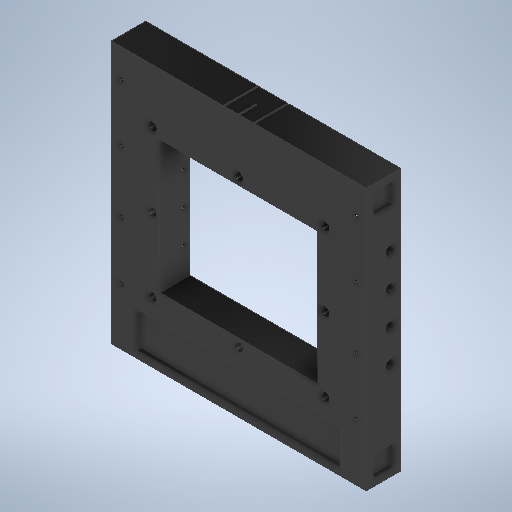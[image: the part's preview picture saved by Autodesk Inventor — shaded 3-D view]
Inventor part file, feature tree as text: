
AUTODESK INVENTOR PART (.ipt)
format: ipt  version: 2025.1 (Build 291241000, 241)  size: 1,624,064 bytes
history: native  units: mm
features: extrude x28, sketch x11, plane x1
ambient origin geometry x8: Origin, YZ Plane, XZ Plane, XY Plane, X Axis, Y Axis, Z Axis, Center Point
bodies: Volumenkörper1 (feature_tree)
feature tree (40):
  extrude  "Extrusion1"  Depth=178.0mm
  extrude  "Extrusion2"  Depth=2.0mm
  extrude  "Extrusion3"  Depth=17.0mm
  extrude  "Extrusion4"  Depth=156.5mm TaperAngle=0.0deg
  extrude  "Extrusion5"  TaperAngle=45.0deg  [1 undecoded]
  extrude  "Extrusion6"  TaperAngle=45.0deg  [1 undecoded]
  extrude  "Extrusion7"  Depth=181.0mm TaperAngle=0.0deg
  extrude  "Extrusion8"  Depth=5.0mm TaperAngle=0.0deg
  plane  "Arbeitsebene1"
  extrude  "Extrusion9"  Depth=5.0mm
  extrude  "Extrusion10"  Depth=150.7mm
  extrude  "Extrusion11"  Depth=3.0mm TaperAngle=0.0deg
  extrude  "Extrusion12"  TaperAngle=0.0deg  [1 undecoded]
  extrude  "Extrusion13"  Depth=5.0mm
  extrude  "Extrusion14"  Depth=5.0mm
  extrude  "Extrusion15"  Depth=5.0mm
  extrude  "Extrusion16"  Depth=5.0mm
  extrude  "Extrusion17"  Depth=3.0mm TaperAngle=0.0deg
  extrude  "Extrusion20"  Depth=5.0mm
  extrude  "Extrusion21"  Depth=5.0mm
  extrude  "Extrusion22"  Depth=5.0mm
  extrude  "Extrusion23"  Depth=5.0mm
  extrude  "Extrusion24"  Depth=3.0mm TaperAngle=0.0deg
  extrude  "Extrusion25"  Depth=3.0mm TaperAngle=0.0deg
  extrude  "Extrusion26"  Depth=5.0mm
  extrude  "Extrusion27"  Depth=5.0mm
  extrude  "Extrusion28"  Depth=3.0mm
  extrude  "Extrusion29"  Depth=3.0mm
  extrude  "Extrusion30"  Depth=5.0mm TaperAngle=0.0deg
  sketch  "Skizze3"  dims[d0=183.0mm d1=178.0mm]
  sketch  "Skizze9"  dims[d2=24.0mm d3=0.0mm d4=2.0mm]
  sketch  "Skizze10"  dims[d5=2.0mm d6=17.0mm]
  sketch  "Skizze11"  dims[d7=24.0mm d8=156.5mm d9=0.0mm]
  sketch  "Skizze12"  dims[d10=5.0mm d11=45.0deg]
  sketch  "Skizze14"  dims[d12=45.0deg d13=45.0deg]
  sketch  "Skizze30"  dims[d14=45.0deg d15=181.0mm d16=0.0mm]
  sketch  "Skizze36"  dims[d17=5.0mm d18=0.0mm d19=2.0mm d20=0.0mm]
  sketch  "Skizze42"  dims[d21=5.0mm d22=24.0mm]
  sketch  "Skizze45"  dims[d23=24.0mm d24=150.7mm]
  sketch  "Skizze47"  dims[d25=133.0mm d26=3.0mm d27=0.0mm d36=0.0mm d37=0.0mm d38=24.0mm d39=24.0mm d40=14.0mm d41=14.0mm d42=3.0mm d43=0.0mm d44=5.0mm d45=24.5mm d46=6.0mm d47=6.0mm d48=3.0mm d49=0.0mm d50=3.0mm d51=0.0mm d52=2.0mm d53=24.5mm d54=3.0mm d55=3.0mm d56=181.0mm d57=0.0mm d58=20.0mm d59=10.0mm d60=10.0mm d61=10.0mm d62=10.0mm d63=10.0mm d64=10.0mm d65=10.0mm d66=10.0mm d67=10.0mm d68=10.0mm d69=10.0mm d70=10.0mm d71=10.0mm d72=8.0mm d73=2.0mm d74=2.0mm d75=8.0mm d76=2.0mm d77=2.0mm d78=114.0mm d79=0.0mm d80=178.0mm d81=14.5mm d82=1.0mm d83=1.0mm d84=154.0mm d85=154.0mm d86=1.0mm d87=0.0mm d88=1.0mm d89=0.0mm d90=130.0mm d91=130.0mm d94=1.0mm d98=3.0mm d99=0.0mm d100=3.0mm d101=0.0mm d102=3.0mm d103=0.0mm d105=92.5mm d106=110.2mm d107=15.0mm d108=15.0mm d109=15.0mm d110=15.0mm d112=3.4mm d113=3.4mm d114=3.4mm d115=3.4mm d116=3.4mm d117=3.4mm d118=3.4mm d119=0.0mm d120=0.0mm d121=0.0mm d122=0.0mm d123=0.0mm d125=0.0mm d126=0.0mm d127=0.0mm d128=0.0mm d129=0.0mm d130=0.0mm d131=3.4mm d132=120.7mm d133=103.0mm d134=2.5mm d140=24.0mm d141=24.0mm d142=24.0mm d143=24.0mm d144=24.0mm d145=24.0mm d146=24.0mm d147=5.0mm d148=0.0mm d161=5.0mm d162=5.0mm d163=5.0mm d164=5.0mm d165=5.0mm d166=5.0mm d167=5.0mm d168=5.0mm d169=14.0mm d170=14.0mm d171=14.0mm d172=14.0mm d173=14.0mm d174=14.0mm d175=14.0mm d176=14.0mm d177=3.0mm d178=0.0mm d179=20.0mm d180=2.0mm d181=2.0mm d182=1.0mm d183=0.0mm d184=20.0mm d185=0.0mm d186=130.0mm d187=14.0mm d188=6.0mm d189=6.0mm d190=6.0mm d191=6.0mm d192=6.0mm d193=6.0mm d194=6.0mm d195=6.0mm d196=20.0mm d197=0.0mm d198=168.5mm d199=0.0mm d200=5.0mm d201=0.0mm d202=5.7mm d203=12.0mm d204=12.0mm d205=20.0mm d206=40.0mm d207=40.0mm d208=40.0mm d209=5.7mm d210=5.7mm d211=5.7mm d212=3.4mm d213=3.4mm d214=3.4mm d215=3.4mm d216=3.4mm d217=3.4mm d218=3.4mm d219=3.4mm d220=0.0mm d221=0.0mm d222=0.0mm d223=0.0mm d224=6.0mm d225=6.0mm d226=6.0mm d227=6.0mm d228=6.0mm d229=6.0mm d230=6.0mm d231=6.0mm d232=10.0mm d233=0.0mm d282=3.0mm d283=3.0mm d284=3.0mm d285=3.0mm d286=10.0mm d287=0.0mm d288=0.0mm d289=6.0mm d290=6.0mm d291=6.0mm d292=6.0mm d293=5.0mm d294=0.0mm d295=5.0mm d296=0.0mm]
note: 3 required parameter values undecoded (feature->parameter linkage not recoverable at this tier; creation-order binding heuristic only, values carry confidence <= 0.55)
